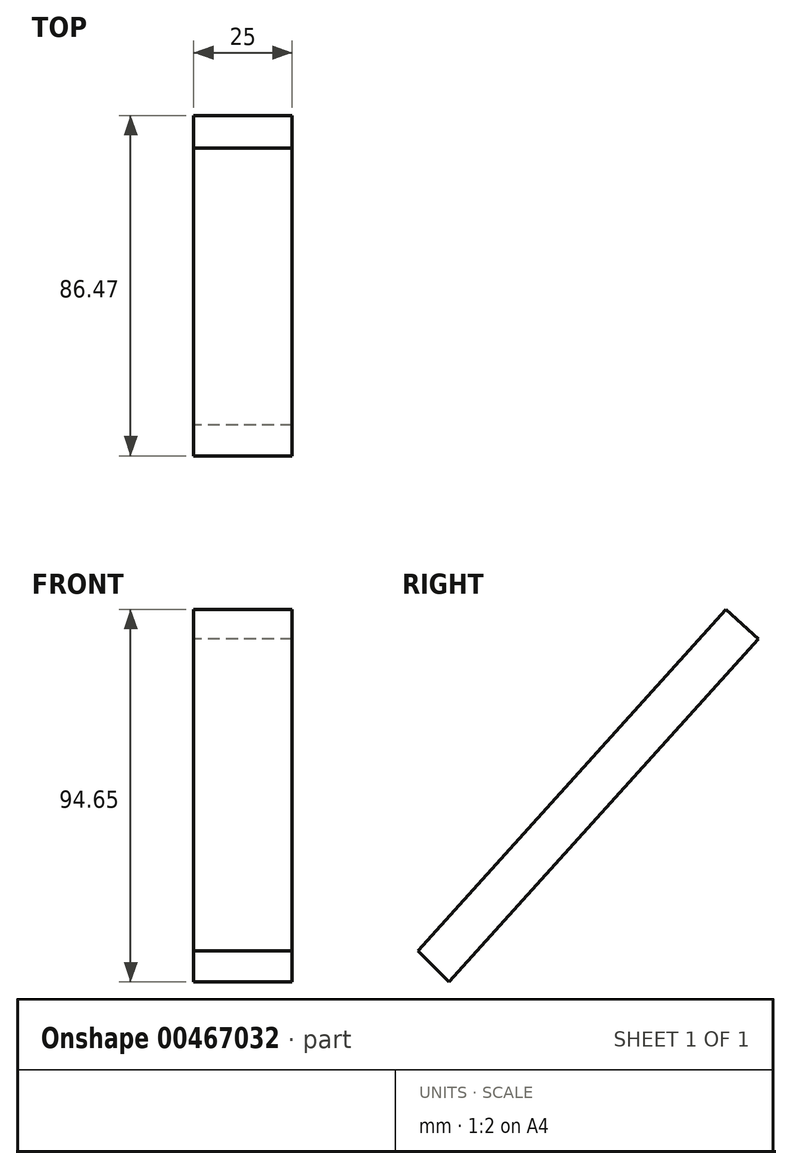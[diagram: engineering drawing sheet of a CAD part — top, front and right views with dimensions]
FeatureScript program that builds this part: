
annotation { "Feature Type Name" : "Feature", "Feature Type Description" : "" }
export const myFeature = defineFeature(function(context is Context, id is Id, definition is map)
    precondition{}
    {
        {
            var Q0;
            Q0=qCreatedBy(makeId("Right.planeOp"),FACE);
            var sketch = newSketch(context, id + "F0", { "sketchPlane" : qUnion([Q0])});
            skLineSegment(sketch, "E0", {"start": v(-45.2, -50.31) * mm, "end": v(33, 36.46) * mm});
            skLineSegment(sketch, "E1", {"start": v(33, 36.46) * mm, "end": v(41.26, 29.01) * mm});
            skLineSegment(sketch, "E2", {"start": v(41.26, 29.01) * mm, "end": v(-37.33, -58.19) * mm});
            skLineSegment(sketch, "E3", {"start": v(-37.33, -58.19) * mm, "end": v(-45.2, -50.31) * mm});
            skSolve(sketch);
        }
        {
            var Q0;
            Q0 = qSketchRegion(id + "F0", true);
            extrude(context, id + "F1", {"entities" : qUnion([Q0]), "depth" : 25 * mm});
        }
    });
